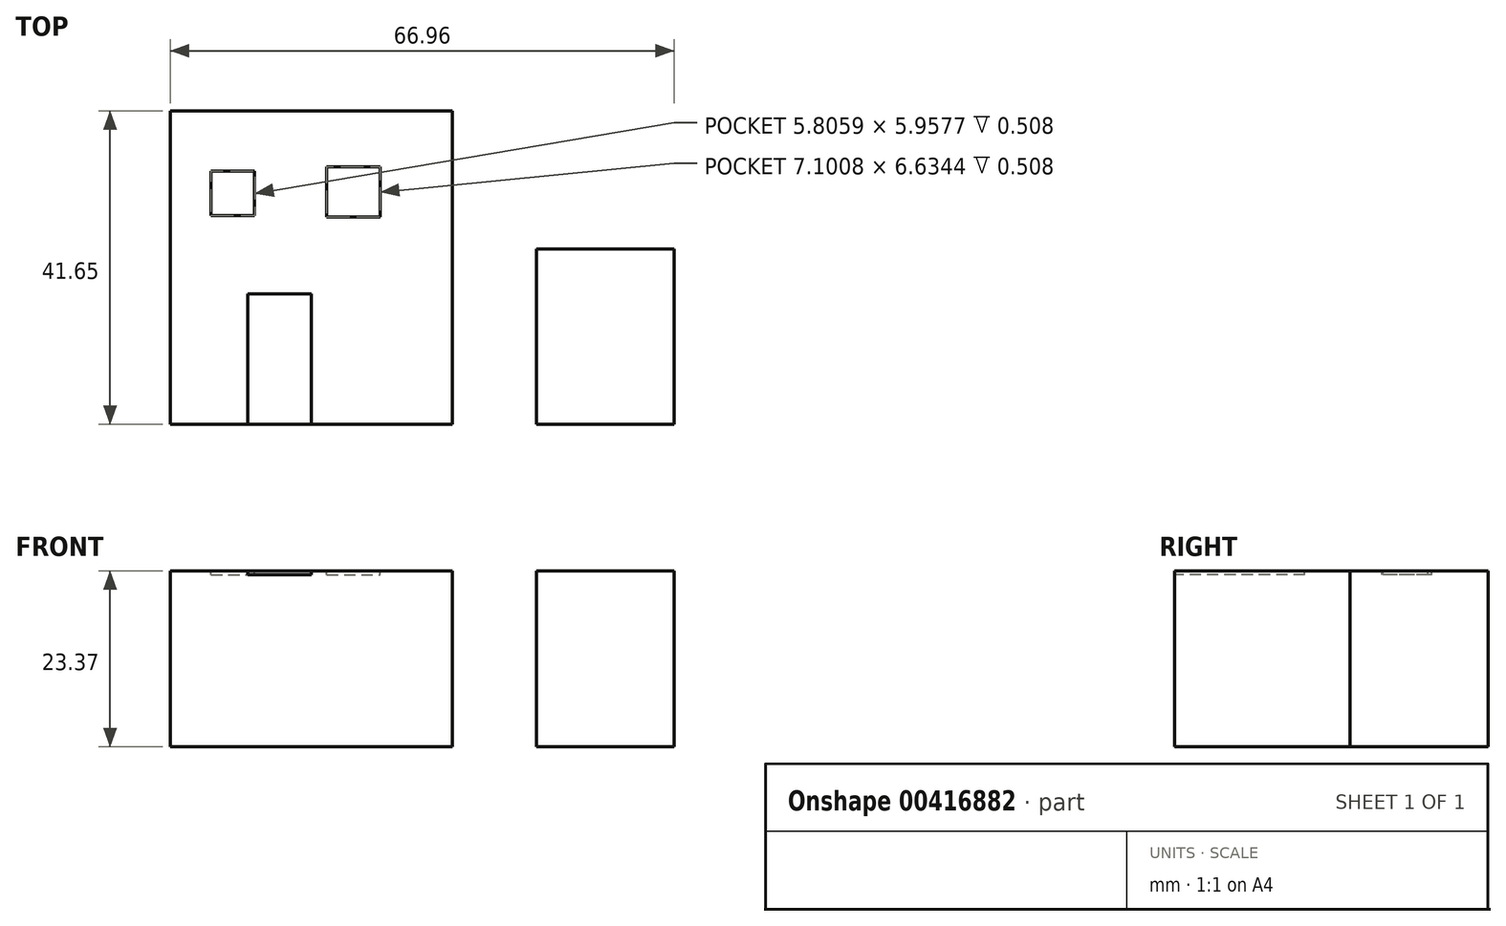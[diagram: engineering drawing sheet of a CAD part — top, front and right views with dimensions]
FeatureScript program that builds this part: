
annotation { "Feature Type Name" : "Feature", "Feature Type Description" : "" }
export const myFeature = defineFeature(function(context is Context, id is Id, definition is map)
    precondition{}
    {
        {
            var Q0;
            Q0=qCreatedBy(makeId("Top.planeOp"),FACE);
            var sketch = newSketch(context, id + "F0", { "sketchPlane" : qUnion([Q0])});
            skLineSegment(sketch, "E0.bottom", {"start": v(45.73, 0) * mm, "end": v(8.27, 0) * mm});
            skLineSegment(sketch, "E0.top", {"start": v(45.73, 41.65) * mm, "end": v(8.27, 41.65) * mm});
            skLineSegment(sketch, "E0.left", {"start": v(45.73, 0) * mm, "end": v(45.73, 41.65) * mm});
            skLineSegment(sketch, "E0.right", {"start": v(8.27, 0) * mm, "end": v(8.27, 41.65) * mm});
            skPoint(sketch, "E0.middle", {"position": v(27, 20.82) * mm});
            skLineSegment(sketch, "E1.bottom", {"start": v(56.9, 0) * mm, "end": v(75.23, 0) * mm});
            skLineSegment(sketch, "E1.top", {"start": v(56.9, 23.32) * mm, "end": v(75.23, 23.32) * mm});
            skLineSegment(sketch, "E1.left", {"start": v(56.9, 0) * mm, "end": v(56.9, 23.32) * mm});
            skLineSegment(sketch, "E1.right", {"start": v(75.23, 0) * mm, "end": v(75.23, 23.32) * mm});
            skPoint(sketch, "E1.middle", {"position": v(66.06, 11.66) * mm});
            skPoint(sketch, "E1.cornerSnap0", {"position": v(27, 0) * mm});
            skSolve(sketch);
        }
        {
            var Q0;
            Q0=makeQuery(id+"F0.imprint","IMPRINT",FACE,{"disambiguationData":[TD([[makeQuery(id+"F0.imprint","IMPRINT",EDGE,{"derivedFrom":sQuery(id+"F0.wireOp",EDGE,"E0.bottom")}),-1.0]])]});
            var Q1;
            Q1=makeQuery(id+"F0.imprint","IMPRINT",FACE,{"disambiguationData":[TD([[makeQuery(id+"F0.imprint","IMPRINT",EDGE,{"derivedFrom":sQuery(id+"F0.wireOp",EDGE,"E1.bottom")}),1.0]])]});
            extrude(context, id + "F1", {"entities" : qUnion([Q0, Q1]), "depth" : 23.37 * mm});
        }
        {
            var Q0;
            Q0=makeQuery(id+"F1.opExtrude","CAP_FACE",FACE,{"disambiguationData":[OSD([sQuery(id+"F0.wireOp",EDGE,"E0.bottom"),sQuery(id+"F0.wireOp",EDGE,"E0.top"),sQuery(id+"F0.wireOp",EDGE,"E0.left"),sQuery(id+"F0.wireOp",EDGE,"E0.right")])],"isStart":false});
            var sketch = newSketch(context, id + "F2", { "sketchPlane" : qUnion([Q0])});
            skLineSegment(sketch, "E2.bottom", {"start": v(13.68, 33.67) * mm, "end": v(19.48, 33.67) * mm});
            skLineSegment(sketch, "E2.top", {"start": v(13.68, 27.72) * mm, "end": v(19.48, 27.72) * mm});
            skLineSegment(sketch, "E2.left", {"start": v(13.68, 33.67) * mm, "end": v(13.68, 27.72) * mm});
            skLineSegment(sketch, "E2.right", {"start": v(19.48, 33.67) * mm, "end": v(19.48, 27.72) * mm});
            skLineSegment(sketch, "E3.bottom", {"start": v(29.06, 34.2) * mm, "end": v(36.16, 34.2) * mm});
            skLineSegment(sketch, "E3.top", {"start": v(29.06, 27.57) * mm, "end": v(36.16, 27.57) * mm});
            skLineSegment(sketch, "E3.left", {"start": v(29.06, 34.2) * mm, "end": v(29.06, 27.57) * mm});
            skLineSegment(sketch, "E3.right", {"start": v(36.16, 34.2) * mm, "end": v(36.16, 27.57) * mm});
            skLineSegment(sketch, "E4.bottom", {"start": v(18.54, 17.32) * mm, "end": v(27, 17.32) * mm});
            skLineSegment(sketch, "E4.top", {"start": v(18.54, 0) * mm, "end": v(27, 0) * mm});
            skLineSegment(sketch, "E4.left", {"start": v(18.54, 17.32) * mm, "end": v(18.54, 0) * mm});
            skLineSegment(sketch, "E4.right", {"start": v(27, 17.32) * mm, "end": v(27, 0) * mm});
            skSolve(sketch);
        }
        {
            var Q0;
            Q0=makeQuery(id+"F2.imprint","IMPRINT",FACE,{"disambiguationData":[TD([[makeQuery(id+"F2.imprint","IMPRINT",EDGE,{"derivedFrom":sQuery(id+"F2.wireOp",EDGE,"E2.bottom")}),-1.0]])]});
            var Q1;
            Q1=makeQuery(id+"F2.imprint","IMPRINT",FACE,{"disambiguationData":[TD([[makeQuery(id+"F2.imprint","IMPRINT",EDGE,{"derivedFrom":sQuery(id+"F2.wireOp",EDGE,"E3.bottom")}),-1.0]])]});
            var Q2;
            Q2=makeQuery(id+"F2.imprint","IMPRINT",FACE,{"disambiguationData":[TD([[makeQuery(id+"F2.imprint","IMPRINT",EDGE,{"derivedFrom":sQuery(id+"F2.wireOp",EDGE,"E4.bottom")}),-1.0]])]});
            extrude(context, id + "F3", {"entities" : qUnion([Q0, Q1, Q2]), "operationType" : NewBodyOperationType.REMOVE, "oppositeDirection" : true, "depth" : 0.5 * mm});
        }
    });
